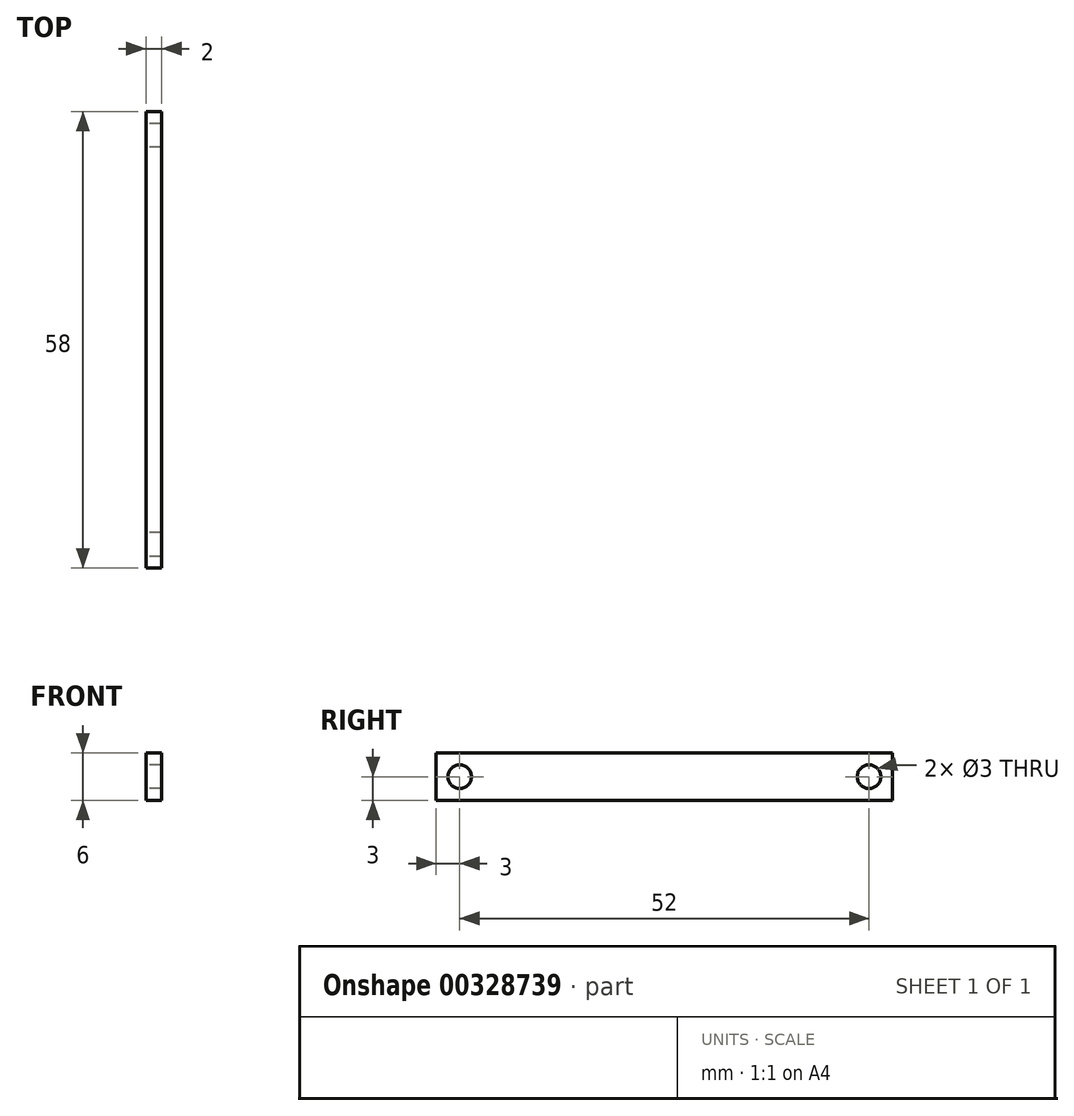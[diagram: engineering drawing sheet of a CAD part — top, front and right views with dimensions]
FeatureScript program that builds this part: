
annotation { "Feature Type Name" : "Feature", "Feature Type Description" : "" }
export const myFeature = defineFeature(function(context is Context, id is Id, definition is map)
    precondition{}
    {
        {
            var Q0;
            Q0=qCreatedBy(makeId("Right.planeOp"),FACE);
            var sketch = newSketch(context, id + "F0", { "sketchPlane" : qUnion([Q0])});
            skLineSegment(sketch, "E0.bottom", {"start": v(29, 3) * mm, "end": v(-29, 3) * mm});
            skLineSegment(sketch, "E0.top", {"start": v(29, -3) * mm, "end": v(-29, -3) * mm});
            skLineSegment(sketch, "E0.left", {"start": v(29, 3) * mm, "end": v(29, -3) * mm});
            skLineSegment(sketch, "E0.right", {"start": v(-29, 3) * mm, "end": v(-29, -3) * mm});
            skPoint(sketch, "E0.middle", {"position": v(0, 0) * mm});
            skLineSegment(sketch, "E1", {"start": v(-29, 0) * mm, "end": v(29, 0) * mm, "construction": true});
            skCircle(sketch, "E2", {"center": v(-26, 0) * mm, "radius": 1.5 * mm});
            skCircle(sketch, "E3", {"center": v(26, 0) * mm, "radius": 1.5 * mm});
            skSolve(sketch);
        }
        {
            var Q0;
            Q0 = qSketchRegion(id + "F0", true);
            extrude(context, id + "F1", {"entities" : qUnion([Q0]), "depth" : 1 * mm, "hasSecondDirection" : true, "secondDirectionOppositeDirection" : true, "secondDirectionDepth" : 1 * mm});
        }
    });
